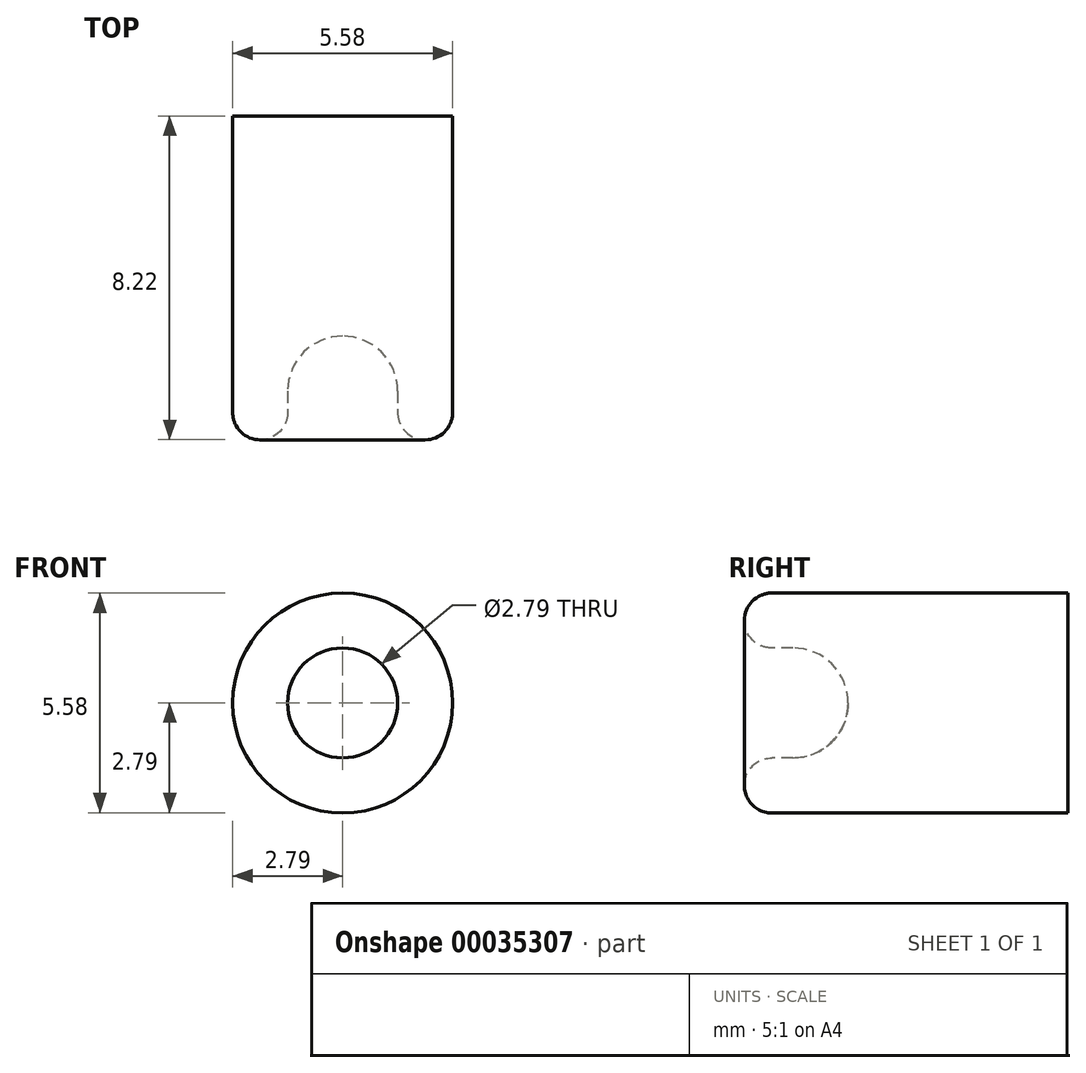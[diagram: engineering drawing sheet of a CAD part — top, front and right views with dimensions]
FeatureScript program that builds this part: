
annotation { "Feature Type Name" : "Feature", "Feature Type Description" : "" }
export const myFeature = defineFeature(function(context is Context, id is Id, definition is map)
    precondition{}
    {
        {
            var Q0;
            Q0=qCreatedBy(makeId("Right.planeOp"),FACE);
            var sketch = newSketch(context, id + "F0", { "sketchPlane" : qUnion([Q0])});
            skPoint(sketch, "E0", {"position": v(-5.18, 2.1) * mm});
            skCircle(sketch, "E1", {"center": v(-5.18, 2.1) * mm, "radius": 0.7 * mm});
            skLineSegment(sketch, "E2", {"start": v(2.35, 2.8) * mm, "end": v(-5.18, 2.8) * mm});
            skLineSegment(sketch, "E3", {"start": v(2.35, 2.8) * mm, "end": v(2.35, 0) * mm});
            skLineSegment(sketch, "E4", {"start": v(2.35, 0) * mm, "end": v(-3.24, 0) * mm});
            skPoint(sketch, "E5", {"position": v(-4.64, 1.4) * mm});
            skArc(sketch, "E6", {"start": v(-3.24, 0) * mm, "mid": v(-3.65, 0.99) * mm, "end": v(-4.64, 1.4) * mm});
            skLineSegment(sketch, "E7", {"start": v(-5.18, 1.4) * mm, "end": v(-4.64, 1.4) * mm});
            skLineSegment(sketch, "E8", {"start": v(-6.34, 0) * mm, "end": v(4.23, 0) * mm, "construction": true});
            skSolve(sketch);
        }
        {
            var Q0;
            {var subQ0=sQuery(id+"F0.wireOp",EDGE,"E1");var subQ2=makeQuery(id+"F0.imprint","INTERSECT",VERTEX,{"derivedFrom":[subQ0,sQuery(id+"F0.wireOp",EDGE,"E2")]});Q0=makeQuery(id+"F0.imprint","IMPRINT",FACE,{"disambiguationData":[TD([[makeQuery(id+"F0.imprint","IMPRINT",EDGE,{"disambiguationData":[TD([[subQ2,-1.0]])],"derivedFrom":subQ0}),1.0]])]});}
            var Q1;
            {var subQ1=sQuery(id+"F0.wireOp",EDGE,"E2");Q1=makeQuery(id+"F0.imprint","IMPRINT",FACE,{"disambiguationData":[TD([[makeQuery(id+"F0.imprint","IMPRINT",EDGE,{"derivedFrom":subQ1}),1.0]])]});}
            var Q2;
            Q2=sQuery(id+"F0.wireOp",EDGE,"E8");
            revolve(context, id + "F1", {"entities" : qUnion([Q0, Q1]), "axis" : qUnion([Q2]), "revolveType" : RevolveType.FULL});
        }
    });
